# Revit family: Salda Indoor Rotor Vertical AHU.Smarty VER
name_source: partatom
category: Mechanical Equipment
revit_build: Autodesk Revit 2016 (Build: 20150220_1215(x64)
units: mm (PartAtom-declared; Revit-internal decimal feet)

## family parameters
Always vertical = Yes
Cut with Voids When Loaded = No
OmniClass Number = 23.75.35.14.11
OmniClass Title = Built-Up Indoor Air Handling Units
Part Type = Normal
Room Calculation Point = No
Round Connector Dimension = Use Diameter
Shared = No
Work Plane-Based = No

## types (2) — shared parameters
Connector Back Horizontal Offset = 98 mm  [stored 0.321522 ft]
Connector Diameters = 125 mm
Connector Front Horizontal Offset = 106 mm
Connector Height = 33 mm  [stored 0.108268 ft]
Current = 4 A
Kitchen Hood Connector Diameter = 175 mm  [stored 0.574147 ft]
L1 = 225 mm
L2 = 100 mm  [stored 0.328084 ft]
L3 = 84 mm  [stored 0.275591 ft]
L4 = 238 mm
Manufacturer = Salda
Module Height = 620 mm  [stored 2.03412 ft]
Overall Height = 653 mm
Overall Length = 598 mm  [stored 1.96194 ft]
Overall Width = 320 mm  [stored 1.04987 ft]
Service Area Width = 640 mm  [stored 2.09974 ft]
URL = http://salda.lt
Unit Mass = 36.00 kg
Voltage = 230 V

## per-type parameters (varying)
| type | Maximum Flow Rate | Power |
| Smarty 2R VER | 250.0 m³/h | 750 W |
| Smarty 2R VER PLUS | 305.0 m³/h | 770 W |

note: column(s) folded — value = type name in every type: Model

note: [stored X ft] marks values corroborated as IEEE doubles in the binary element streams (Revit-internal decimal feet)

## geometry (parser evidence)
native form markers: Sweep x8
no freeform markers — native parametric forms only
